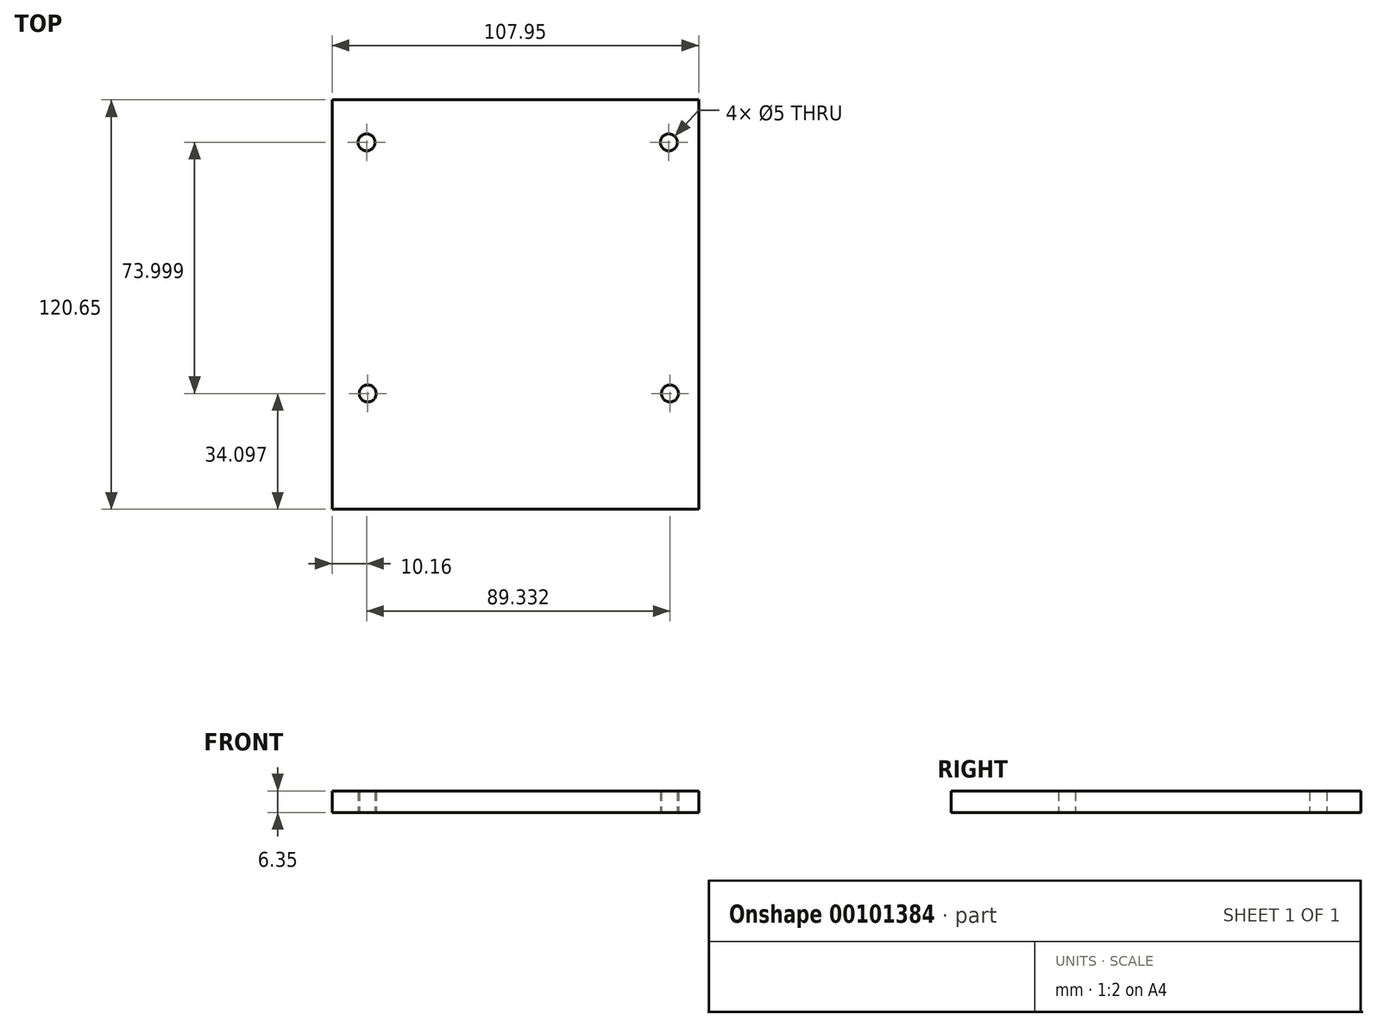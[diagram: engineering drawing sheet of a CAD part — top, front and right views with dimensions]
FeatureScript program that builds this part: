
annotation { "Feature Type Name" : "Feature", "Feature Type Description" : "" }
export const myFeature = defineFeature(function(context is Context, id is Id, definition is map)
    precondition{}
    {
        {
            var Q0;
            Q0=qCreatedBy(makeId("Top.planeOp"),FACE);
            var sketch = newSketch(context, id + "F0", { "sketchPlane" : qUnion([Q0])});
            skLineSegment(sketch, "E0.bottom", {"start": v(0, 0) * mm, "end": v(107.95, 0) * mm});
            skLineSegment(sketch, "E0.top", {"start": v(0, 120.65) * mm, "end": v(107.95, 120.65) * mm});
            skLineSegment(sketch, "E0.left", {"start": v(0, 0) * mm, "end": v(0, 120.65) * mm});
            skLineSegment(sketch, "E0.right", {"start": v(107.95, 0) * mm, "end": v(107.95, 120.65) * mm});
            skLineSegment(sketch, "E1.bottom", {"start": v(15.88, 0) * mm, "end": v(28.58, 0) * mm});
            skLineSegment(sketch, "E1.top", {"start": v(15.88, -6.35) * mm, "end": v(28.58, -6.35) * mm});
            skLineSegment(sketch, "E1.left", {"start": v(15.88, 0) * mm, "end": v(15.88, -6.35) * mm});
            skLineSegment(sketch, "E1.right", {"start": v(28.58, 0) * mm, "end": v(28.58, -6.35) * mm});
            skLineSegment(sketch, "E2.bottom", {"start": v(92.08, 0) * mm, "end": v(79.38, 0) * mm});
            skLineSegment(sketch, "E2.top", {"start": v(92.08, -6.35) * mm, "end": v(79.38, -6.35) * mm});
            skLineSegment(sketch, "E2.left", {"start": v(92.08, 0) * mm, "end": v(92.08, -6.35) * mm});
            skLineSegment(sketch, "E2.right", {"start": v(79.38, 0) * mm, "end": v(79.38, -6.35) * mm});
            skLineSegment(sketch, "E3.0.1.0", {"start": v(15.88, 120.65) * mm, "end": v(28.58, 120.65) * mm});
            skLineSegment(sketch, "E3.0.1.1", {"start": v(92.08, 120.65) * mm, "end": v(79.38, 120.65) * mm});
            skLineSegment(sketch, "E3.0.1.2", {"start": v(79.38, 127) * mm, "end": v(79.38, 120.65) * mm});
            skLineSegment(sketch, "E3.0.1.3", {"start": v(92.08, 127) * mm, "end": v(79.38, 127) * mm});
            skLineSegment(sketch, "E3.0.1.4", {"start": v(92.08, 127) * mm, "end": v(92.08, 120.65) * mm});
            skLineSegment(sketch, "E3.0.1.5", {"start": v(28.58, 127) * mm, "end": v(28.58, 120.65) * mm});
            skLineSegment(sketch, "E3.0.1.6", {"start": v(15.88, 127) * mm, "end": v(28.58, 127) * mm});
            skLineSegment(sketch, "E3.0.1.7", {"start": v(15.88, 127) * mm, "end": v(15.88, 120.65) * mm});
            skLineSegment(sketch, "E3.direction1", {"start": v(15.88, -6.35) * mm, "end": v(41.28, -6.35) * mm, "construction": true});
            skLineSegment(sketch, "E3.direction2", {"start": v(15.88, -6.35) * mm, "end": v(15.88, 120.65) * mm, "construction": true});
            skCircle(sketch, "E4", {"center": v(99.16, 108.1) * mm, "radius": 2.5 * mm});
            skCircle(sketch, "E5", {"center": v(10.16, 108.1) * mm, "radius": 2.5 * mm});
            skCircle(sketch, "E6.0.1.0", {"center": v(99.5, 34.1) * mm, "radius": 2.5 * mm});
            skCircle(sketch, "E6.0.1.1", {"center": v(10.5, 34.1) * mm, "radius": 2.5 * mm});
            skLineSegment(sketch, "E6.direction1", {"start": v(99.16, 108.1) * mm, "end": v(124.56, 108.1) * mm, "construction": true});
            skLineSegment(sketch, "E6.direction2", {"start": v(99.16, 108.1) * mm, "end": v(99.5, 34.1) * mm, "construction": true});
            skSolve(sketch);
        }
        {
            var Q0;
            {var subQ1=sQuery(id+"F0.wireOp",EDGE,"E0.left");Q0=makeQuery(id+"F0.imprint","IMPRINT",FACE,{"disambiguationData":[TD([[makeQuery(id+"F0.imprint","IMPRINT",EDGE,{"derivedFrom":subQ1}),-1.0]])]});}
            var Q1;
            Q1=makeQuery(id+"F0.imprint","IMPRINT",FACE,{"disambiguationData":[TD([[makeQuery(id+"F0.imprint","IMPRINT",EDGE,{"derivedFrom":sQuery(id+"F0.wireOp",EDGE,"E3.0.1.0")}),1.0]])]});
            var Q2;
            Q2=makeQuery(id+"F0.imprint","IMPRINT",FACE,{"disambiguationData":[TD([[makeQuery(id+"F0.imprint","IMPRINT",EDGE,{"derivedFrom":sQuery(id+"F0.wireOp",EDGE,"E3.0.1.1")}),-1.0]])]});
            var Q3;
            Q3=makeQuery(id+"F0.imprint","IMPRINT",FACE,{"disambiguationData":[TD([[makeQuery(id+"F0.imprint","IMPRINT",EDGE,{"derivedFrom":sQuery(id+"F0.wireOp",EDGE,"E2.bottom")}),1.0]])]});
            var Q4;
            Q4=makeQuery(id+"F0.imprint","IMPRINT",FACE,{"disambiguationData":[TD([[makeQuery(id+"F0.imprint","IMPRINT",EDGE,{"derivedFrom":sQuery(id+"F0.wireOp",EDGE,"E1.bottom")}),-1.0]])]});
            extrude(context, id + "F1", {"entities" : qUnion([Q0, Q1, Q2, Q3, Q4]), "depth" : 6.35 * mm});
        }
    });
